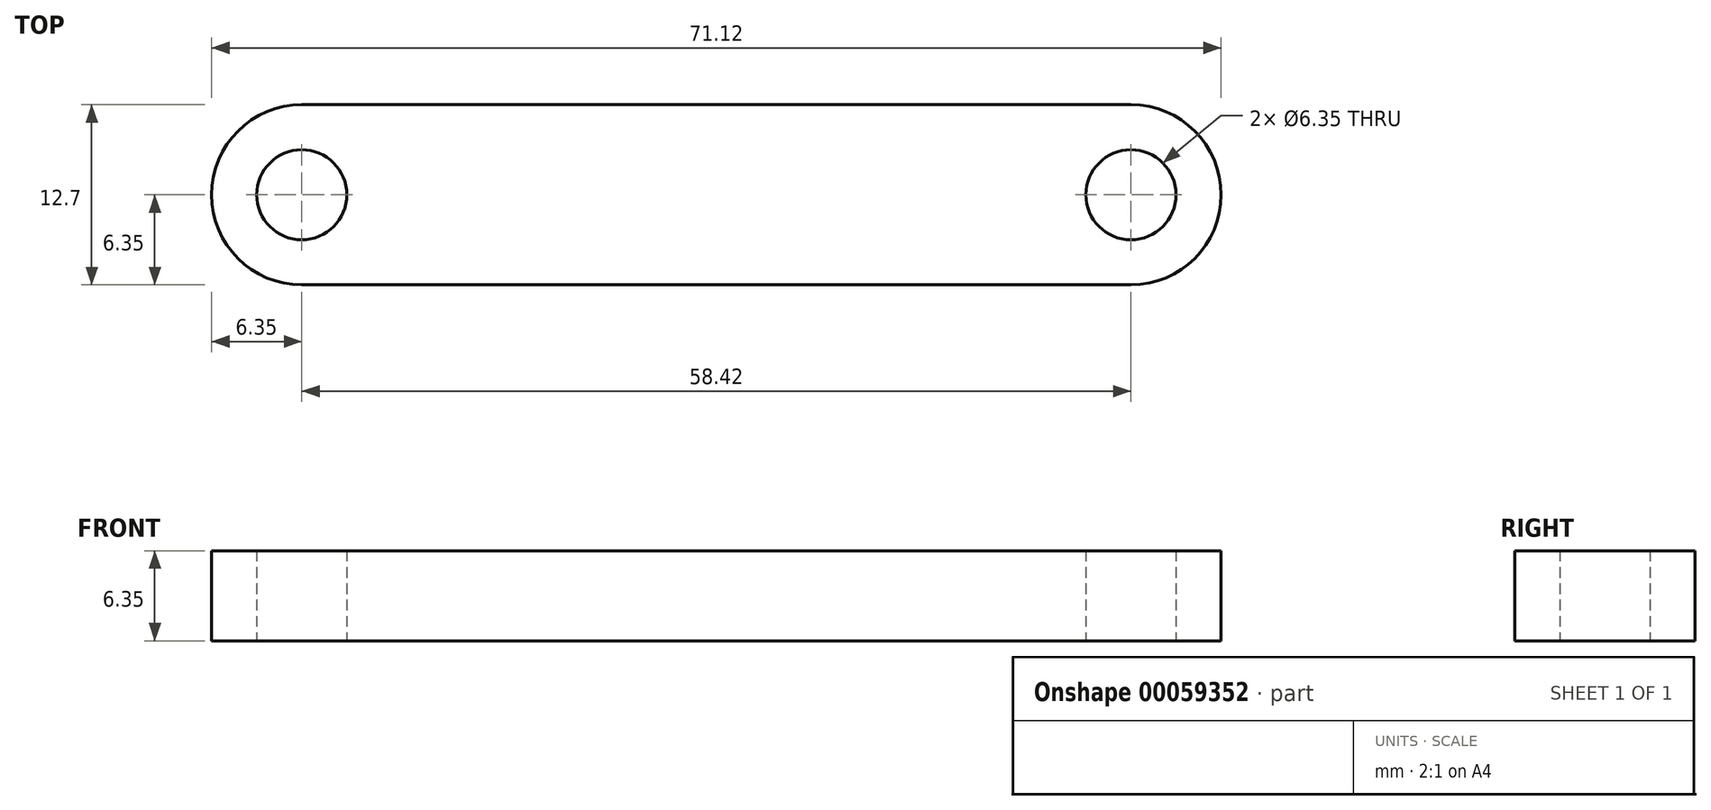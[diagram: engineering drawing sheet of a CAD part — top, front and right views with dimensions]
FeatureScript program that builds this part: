
annotation { "Feature Type Name" : "Feature", "Feature Type Description" : "" }
export const myFeature = defineFeature(function(context is Context, id is Id, definition is map)
    precondition{}
    {
        {
            var Q0;
            Q0=qCreatedBy(makeId("Top.planeOp"),FACE);
            var sketch = newSketch(context, id + "F0", { "sketchPlane" : qUnion([Q0])});
            skArc(sketch, "E0", {"start": v(0, -6.35) * mm, "mid": v(6.35, 0) * mm, "end": v(0, 6.35) * mm});
            skArc(sketch, "E1", {"start": v(-58.42, 6.35) * mm, "mid": v(-64.77, 0) * mm, "end": v(-58.42, -6.35) * mm});
            skLineSegment(sketch, "E2", {"start": v(-58.42, 6.35) * mm, "end": v(0, 6.35) * mm});
            skLineSegment(sketch, "E3", {"start": v(-58.42, -6.35) * mm, "end": v(0, -6.35) * mm});
            skCircle(sketch, "E4", {"center": v(-58.42, 0) * mm, "radius": 3.18 * mm});
            skCircle(sketch, "E5", {"center": v(0, 0) * mm, "radius": 3.18 * mm});
            skSolve(sketch);
        }
        {
            var Q0;
            Q0=makeQuery(id+"F0.imprint","IMPRINT",FACE,{"disambiguationData":[TD([[makeQuery(id+"F0.imprint","IMPRINT",EDGE,{"derivedFrom":sQuery(id+"F0.wireOp",EDGE,"E0")}),1.0]])]});
            extrude(context, id + "F1", {"entities" : qUnion([Q0]), "depth" : 6.35 * mm});
        }
    });
